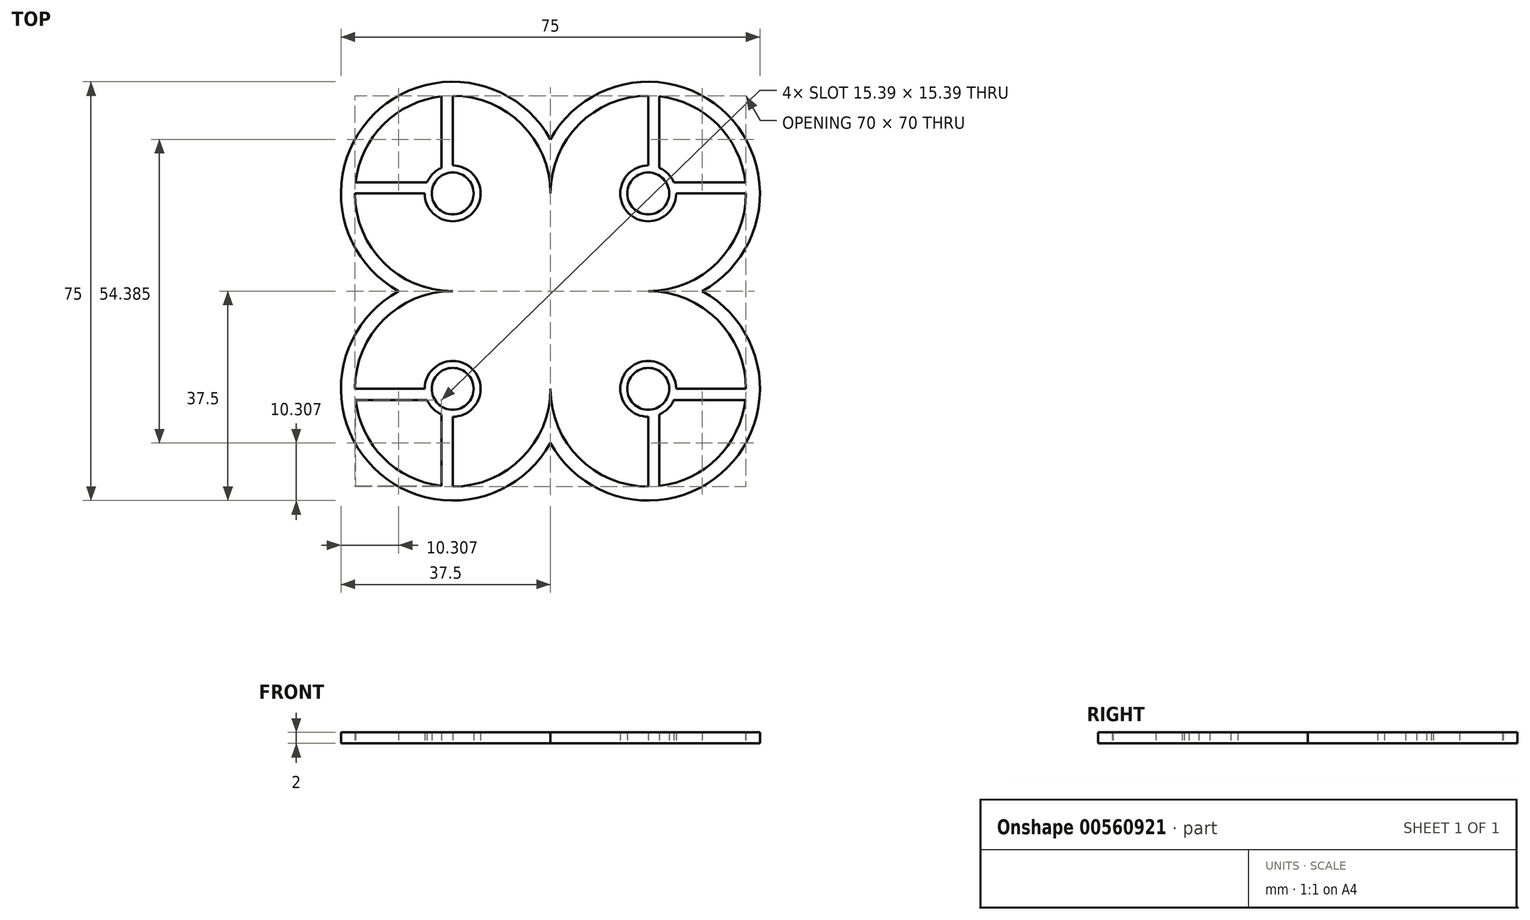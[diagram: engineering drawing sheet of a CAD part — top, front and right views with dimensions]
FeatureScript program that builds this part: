
annotation { "Feature Type Name" : "Feature", "Feature Type Description" : "" }
export const myFeature = defineFeature(function(context is Context, id is Id, definition is map)
    precondition{}
    {
        {
            var Q0;
            Q0=qCreatedBy(makeId("Top.planeOp"),FACE);
            var sketch = newSketch(context, id + "F0", { "sketchPlane" : qUnion([Q0])});
            skCircle(sketch, "E0", {"center": v(-17.5, 17.5) * mm, "radius": 17.5 * mm});
            skCircle(sketch, "E1", {"center": v(17.5, 17.5) * mm, "radius": 17.5 * mm});
            skCircle(sketch, "E2", {"center": v(-17.5, -17.5) * mm, "radius": 17.5 * mm});
            skCircle(sketch, "E3", {"center": v(17.5, -17.5) * mm, "radius": 17.5 * mm});
            skCircle(sketch, "E4", {"center": v(-17.5, 17.5) * mm, "radius": 20 * mm});
            skCircle(sketch, "E5", {"center": v(17.5, 17.5) * mm, "radius": 20 * mm});
            skCircle(sketch, "E6", {"center": v(17.5, -17.5) * mm, "radius": 20 * mm});
            skCircle(sketch, "E7", {"center": v(-17.5, -17.5) * mm, "radius": 20 * mm});
            skCircle(sketch, "E8", {"center": v(17.5, -17.5) * mm, "radius": 3.75 * mm});
            skCircle(sketch, "E9", {"center": v(17.5, 17.5) * mm, "radius": 3.75 * mm});
            skCircle(sketch, "E10", {"center": v(-17.5, 17.5) * mm, "radius": 3.75 * mm});
            skCircle(sketch, "E11", {"center": v(-17.5, -17.5) * mm, "radius": 3.75 * mm});
            skCircle(sketch, "E12", {"center": v(-17.5, -17.5) * mm, "radius": 5 * mm});
            skCircle(sketch, "E13", {"center": v(17.5, -17.5) * mm, "radius": 5 * mm});
            skCircle(sketch, "E14", {"center": v(17.5, 17.5) * mm, "radius": 5 * mm});
            skCircle(sketch, "E15", {"center": v(-17.5, 17.5) * mm, "radius": 5 * mm});
            skLineSegment(sketch, "E16.bottom", {"start": v(-17.5, 17.5) * mm, "end": v(-43.31, 17.5) * mm});
            skLineSegment(sketch, "E16.top", {"start": v(-17.5, 41.1) * mm, "end": v(-43.31, 41.1) * mm});
            skLineSegment(sketch, "E16.left", {"start": v(-17.5, 17.5) * mm, "end": v(-17.5, 41.1) * mm});
            skLineSegment(sketch, "E16.right", {"start": v(-43.31, 17.5) * mm, "end": v(-43.31, 41.1) * mm});
            skLineSegment(sketch, "E17.bottom", {"start": v(-22.08, 19.5) * mm, "end": v(-37.86, 19.5) * mm});
            skLineSegment(sketch, "E17.top", {"start": v(-19.5, 36.72) * mm, "end": v(-37.86, 36.72) * mm});
            skLineSegment(sketch, "E17.left", {"start": v(-19.5, 22.08) * mm, "end": v(-19.5, 36.72) * mm});
            skLineSegment(sketch, "E17.right", {"start": v(-37.86, 19.5) * mm, "end": v(-37.86, 36.72) * mm});
            skLineSegment(sketch, "E18.MirrorCS", {"start": v(22.08, 19.5) * mm, "end": v(37.86, 19.5) * mm});
            skLineSegment(sketch, "E19.MirrorCS", {"start": v(19.5, 22.08) * mm, "end": v(19.5, 36.72) * mm});
            skLineSegment(sketch, "E20.MirrorCS", {"start": v(-19.5, -22.08) * mm, "end": v(-19.5, -36.72) * mm});
            skLineSegment(sketch, "E21.MirrorCS", {"start": v(-22.08, -19.5) * mm, "end": v(-37.86, -19.5) * mm});
            skLineSegment(sketch, "E22.MirrorCS", {"start": v(22.08, -19.5) * mm, "end": v(37.86, -19.5) * mm});
            skLineSegment(sketch, "E23.MirrorCS", {"start": v(19.5, -22.08) * mm, "end": v(19.5, -36.72) * mm});
            skLineSegment(sketch, "E24.MirrorCS", {"start": v(17.5, 17.5) * mm, "end": v(17.5, 41.1) * mm});
            skLineSegment(sketch, "E25.MirrorCS", {"start": v(17.5, 17.5) * mm, "end": v(43.31, 17.5) * mm});
            skLineSegment(sketch, "E26.MirrorCS", {"start": v(-17.5, -17.5) * mm, "end": v(-43.31, -17.5) * mm});
            skLineSegment(sketch, "E27.MirrorCS", {"start": v(-17.5, -17.5) * mm, "end": v(-17.5, -41.1) * mm});
            skLineSegment(sketch, "E28.MirrorCS", {"start": v(17.5, -17.5) * mm, "end": v(17.5, -41.1) * mm});
            skLineSegment(sketch, "E29.MirrorCS", {"start": v(17.5, -17.5) * mm, "end": v(43.31, -17.5) * mm});
            skSolve(sketch);
        }
        {
            var Q0;
            {var subQ0=sQuery(id+"F0.wireOp",EDGE,"E5");var subQ1=sQuery(id+"F0.wireOp",EDGE,"E0");var subQ2=makeQuery(id+"F0.imprint","INTERSECT",VERTEX,{"disambiguationData":[OD(0.0)],"derivedFrom":[subQ1,subQ0]});Q0=makeQuery(id+"F0.imprint","IMPRINT",FACE,{"disambiguationData":[TD([[makeQuery(id+"F0.imprint","IMPRINT",EDGE,{"disambiguationData":[TD([[subQ2,-1.0]])],"derivedFrom":subQ1}),-1.0]])]});}
            var Q1;
            {var subQ0=sQuery(id+"F0.wireOp",EDGE,"E4");var subQ1=sQuery(id+"F0.wireOp",EDGE,"E2");var subQ2=makeQuery(id+"F0.imprint","INTERSECT",VERTEX,{"disambiguationData":[OD(1.0)],"derivedFrom":[subQ1,subQ0]});Q1=makeQuery(id+"F0.imprint","IMPRINT",FACE,{"disambiguationData":[TD([[makeQuery(id+"F0.imprint","IMPRINT",EDGE,{"disambiguationData":[TD([[subQ2,-1.0]])],"derivedFrom":subQ1}),-1.0]])]});}
            var Q2;
            {var subQ0=sQuery(id+"F0.wireOp",EDGE,"E5");var subQ1=sQuery(id+"F0.wireOp",EDGE,"E3");var subQ2=makeQuery(id+"F0.imprint","INTERSECT",VERTEX,{"disambiguationData":[OD(0.0)],"derivedFrom":[subQ1,subQ0]});Q2=makeQuery(id+"F0.imprint","IMPRINT",FACE,{"disambiguationData":[TD([[makeQuery(id+"F0.imprint","IMPRINT",EDGE,{"disambiguationData":[TD([[subQ2,1.0]])],"derivedFrom":subQ1}),-1.0]])]});}
            var Q3;
            {var subQ0=sQuery(id+"F0.wireOp",EDGE,"E4");var subQ1=sQuery(id+"F0.wireOp",EDGE,"E1");var subQ2=makeQuery(id+"F0.imprint","INTERSECT",VERTEX,{"disambiguationData":[OD(0.0)],"derivedFrom":[subQ1,subQ0]});Q3=makeQuery(id+"F0.imprint","IMPRINT",FACE,{"disambiguationData":[TD([[makeQuery(id+"F0.imprint","IMPRINT",EDGE,{"disambiguationData":[TD([[subQ2,1.0]])],"derivedFrom":subQ1}),-1.0]])]});}
            var Q4;
            {var subQ0=sQuery(id+"F0.wireOp",EDGE,"E3");var subQ1=sQuery(id+"F0.wireOp",EDGE,"E1");var subQ2=makeQuery(id+"F0.imprint","INTERSECT",VERTEX,{"derivedFrom":[subQ1,subQ0]});Q4=makeQuery(id+"F0.imprint","IMPRINT",FACE,{"disambiguationData":[TD([[makeQuery(id+"F0.imprint","IMPRINT",EDGE,{"disambiguationData":[TD([[subQ2,-1.0]])],"derivedFrom":subQ1}),-1.0]])]});}
            var Q5;
            {var subQ0=sQuery(id+"F0.wireOp",EDGE,"E3");var subQ1=sQuery(id+"F0.wireOp",EDGE,"E2");var subQ2=makeQuery(id+"F0.imprint","INTERSECT",VERTEX,{"derivedFrom":[subQ1,subQ0]});Q5=makeQuery(id+"F0.imprint","IMPRINT",FACE,{"disambiguationData":[TD([[makeQuery(id+"F0.imprint","IMPRINT",EDGE,{"disambiguationData":[TD([[subQ2,1.0]])],"derivedFrom":subQ1}),-1.0]])]});}
            var Q6;
            {var subQ0=sQuery(id+"F0.wireOp",EDGE,"E7");var subQ1=sQuery(id+"F0.wireOp",EDGE,"E0");var subQ2=makeQuery(id+"F0.imprint","INTERSECT",VERTEX,{"disambiguationData":[OD(0.0)],"derivedFrom":[subQ1,subQ0]});Q6=makeQuery(id+"F0.imprint","IMPRINT",FACE,{"disambiguationData":[TD([[makeQuery(id+"F0.imprint","IMPRINT",EDGE,{"disambiguationData":[TD([[subQ2,-1.0]])],"derivedFrom":subQ1}),-1.0]])]});}
            var Q7;
            {var subQ0=sQuery(id+"F0.wireOp",EDGE,"E5");var subQ1=sQuery(id+"F0.wireOp",EDGE,"E0");var subQ2=makeQuery(id+"F0.imprint","INTERSECT",VERTEX,{"disambiguationData":[OD(0.0)],"derivedFrom":[subQ1,subQ0]});Q7=makeQuery(id+"F0.imprint","IMPRINT",FACE,{"disambiguationData":[TD([[makeQuery(id+"F0.imprint","IMPRINT",EDGE,{"disambiguationData":[TD([[subQ2,1.0]])],"derivedFrom":subQ1}),-1.0]])]});}
            var Q8;
            {var subQ0=sQuery(id+"F0.wireOp",EDGE,"E16.bottom");var subQ1=sQuery(id+"F0.wireOp",EDGE,"E0");var subQ2=makeQuery(id+"F0.imprint","INTERSECT",VERTEX,{"derivedFrom":[subQ1,subQ0]});Q8=makeQuery(id+"F0.imprint","IMPRINT",FACE,{"disambiguationData":[TD([[makeQuery(id+"F0.imprint","IMPRINT",EDGE,{"disambiguationData":[TD([[subQ2,-1.0]])],"derivedFrom":subQ1}),-1.0]])]});}
            var Q9;
            {var subQ0=sQuery(id+"F0.wireOp",EDGE,"E17.left");var subQ5=sQuery(id+"F0.wireOp",EDGE,"E0");var subQ6=makeQuery(id+"F0.imprint","INTERSECT",VERTEX,{"derivedFrom":[subQ5,subQ0]});Q9=makeQuery(id+"F0.imprint","IMPRINT",FACE,{"disambiguationData":[TD([[makeQuery(id+"F0.imprint","IMPRINT",EDGE,{"disambiguationData":[TD([[subQ6,-1.0]])],"derivedFrom":subQ5}),-1.0]])]});}
            var Q10;
            {var subQ0=sQuery(id+"F0.wireOp",EDGE,"E17.bottom");var subQ1=sQuery(id+"F0.wireOp",EDGE,"E0");var subQ2=makeQuery(id+"F0.imprint","INTERSECT",VERTEX,{"derivedFrom":[subQ1,subQ0]});Q10=makeQuery(id+"F0.imprint","IMPRINT",FACE,{"disambiguationData":[TD([[makeQuery(id+"F0.imprint","IMPRINT",EDGE,{"disambiguationData":[TD([[subQ2,-1.0]])],"derivedFrom":subQ1}),-1.0]])]});}
            var Q11;
            {var subQ0=sQuery(id+"F0.wireOp",EDGE,"E17.bottom");var subQ1=sQuery(id+"F0.wireOp",EDGE,"E0");var subQ2=makeQuery(id+"F0.imprint","INTERSECT",VERTEX,{"derivedFrom":[subQ1,subQ0]});Q11=makeQuery(id+"F0.imprint","IMPRINT",FACE,{"disambiguationData":[TD([[makeQuery(id+"F0.imprint","IMPRINT",EDGE,{"disambiguationData":[TD([[subQ2,-1.0]])],"derivedFrom":subQ1}),1.0]])]});}
            var Q12;
            {var subQ2=sQuery(id+"F0.wireOp",EDGE,"E16.bottom");var subQ7=sQuery(id+"F0.wireOp",EDGE,"E10");var subQ9=makeQuery(id+"F0.imprint","INTERSECT",VERTEX,{"derivedFrom":[subQ7,subQ2]});Q12=makeQuery(id+"F0.imprint","IMPRINT",FACE,{"disambiguationData":[TD([[makeQuery(id+"F0.imprint","IMPRINT",EDGE,{"disambiguationData":[TD([[subQ9,1.0]])],"derivedFrom":subQ7}),-1.0]])]});}
            var Q13;
            {var subQ0=sQuery(id+"F0.wireOp",EDGE,"E16.left");var subQ1=sQuery(id+"F0.wireOp",EDGE,"E0");var subQ2=makeQuery(id+"F0.imprint","INTERSECT",VERTEX,{"derivedFrom":[subQ1,subQ0]});Q13=makeQuery(id+"F0.imprint","IMPRINT",FACE,{"disambiguationData":[TD([[makeQuery(id+"F0.imprint","IMPRINT",EDGE,{"disambiguationData":[TD([[subQ2,-1.0]])],"derivedFrom":subQ1}),1.0]])]});}
            var Q14;
            {var subQ0=sQuery(id+"F0.wireOp",EDGE,"E16.bottom");var subQ1=sQuery(id+"F0.wireOp",EDGE,"E10");var subQ2=makeQuery(id+"F0.imprint","INTERSECT",VERTEX,{"derivedFrom":[subQ1,subQ0]});Q14=makeQuery(id+"F0.imprint","IMPRINT",FACE,{"disambiguationData":[TD([[makeQuery(id+"F0.imprint","IMPRINT",EDGE,{"disambiguationData":[TD([[subQ2,-1.0]])],"derivedFrom":subQ1}),-1.0]])]});}
            var Q15;
            {var subQ5=sQuery(id+"F0.wireOp",EDGE,"E16.left");var subQ7=sQuery(id+"F0.wireOp",EDGE,"E0");var subQ8=makeQuery(id+"F0.imprint","INTERSECT",VERTEX,{"derivedFrom":[subQ7,subQ5]});Q15=makeQuery(id+"F0.imprint","IMPRINT",FACE,{"disambiguationData":[TD([[makeQuery(id+"F0.imprint","IMPRINT",EDGE,{"disambiguationData":[TD([[subQ8,-1.0]])],"derivedFrom":subQ7}),-1.0]])]});}
            var Q16;
            {var subQ0=sQuery(id+"F0.wireOp",EDGE,"E26.MirrorCS");var subQ1=sQuery(id+"F0.wireOp",EDGE,"E2");var subQ2=makeQuery(id+"F0.imprint","INTERSECT",VERTEX,{"derivedFrom":[subQ1,subQ0]});Q16=makeQuery(id+"F0.imprint","IMPRINT",FACE,{"disambiguationData":[TD([[makeQuery(id+"F0.imprint","IMPRINT",EDGE,{"disambiguationData":[TD([[subQ2,-1.0]])],"derivedFrom":subQ1}),-1.0]])]});}
            var Q17;
            {var subQ0=sQuery(id+"F0.wireOp",EDGE,"E26.MirrorCS");var subQ1=sQuery(id+"F0.wireOp",EDGE,"E2");var subQ2=makeQuery(id+"F0.imprint","INTERSECT",VERTEX,{"derivedFrom":[subQ1,subQ0]});Q17=makeQuery(id+"F0.imprint","IMPRINT",FACE,{"disambiguationData":[TD([[makeQuery(id+"F0.imprint","IMPRINT",EDGE,{"disambiguationData":[TD([[subQ2,-1.0]])],"derivedFrom":subQ1}),1.0]])]});}
            var Q18;
            {var subQ3=sQuery(id+"F0.wireOp",EDGE,"E2");var subQ5=makeQuery(id+"F0.imprint","INTERSECT",VERTEX,{"derivedFrom":[subQ3,sQuery(id+"F0.wireOp",EDGE,"E20.MirrorCS")]});Q18=makeQuery(id+"F0.imprint","IMPRINT",FACE,{"disambiguationData":[TD([[makeQuery(id+"F0.imprint","IMPRINT",EDGE,{"disambiguationData":[TD([[subQ5,1.0]])],"derivedFrom":subQ3}),-1.0]])]});}
            var Q19;
            {var subQ5=sQuery(id+"F0.wireOp",EDGE,"E26.MirrorCS");var subQ7=sQuery(id+"F0.wireOp",EDGE,"E11");var subQ8=makeQuery(id+"F0.imprint","INTERSECT",VERTEX,{"derivedFrom":[subQ7,subQ5]});Q19=makeQuery(id+"F0.imprint","IMPRINT",FACE,{"disambiguationData":[TD([[makeQuery(id+"F0.imprint","IMPRINT",EDGE,{"disambiguationData":[TD([[subQ8,-1.0]])],"derivedFrom":subQ7}),-1.0]])]});}
            var Q20;
            {var subQ0=sQuery(id+"F0.wireOp",EDGE,"E20.MirrorCS");var subQ1=sQuery(id+"F0.wireOp",EDGE,"E2");var subQ2=makeQuery(id+"F0.imprint","INTERSECT",VERTEX,{"derivedFrom":[subQ1,subQ0]});Q20=makeQuery(id+"F0.imprint","IMPRINT",FACE,{"disambiguationData":[TD([[makeQuery(id+"F0.imprint","IMPRINT",EDGE,{"disambiguationData":[TD([[subQ2,-1.0]])],"derivedFrom":subQ1}),1.0]])]});}
            var Q21;
            {var subQ0=sQuery(id+"F0.wireOp",EDGE,"E26.MirrorCS");var subQ1=sQuery(id+"F0.wireOp",EDGE,"E11");var subQ2=makeQuery(id+"F0.imprint","INTERSECT",VERTEX,{"derivedFrom":[subQ1,subQ0]});Q21=makeQuery(id+"F0.imprint","IMPRINT",FACE,{"disambiguationData":[TD([[makeQuery(id+"F0.imprint","IMPRINT",EDGE,{"disambiguationData":[TD([[subQ2,1.0]])],"derivedFrom":subQ1}),-1.0]])]});}
            var Q22;
            {var subQ0=sQuery(id+"F0.wireOp",EDGE,"E27.MirrorCS");var subQ1=sQuery(id+"F0.wireOp",EDGE,"E2");var subQ2=makeQuery(id+"F0.imprint","INTERSECT",VERTEX,{"derivedFrom":[subQ1,subQ0]});Q22=makeQuery(id+"F0.imprint","IMPRINT",FACE,{"disambiguationData":[TD([[makeQuery(id+"F0.imprint","IMPRINT",EDGE,{"disambiguationData":[TD([[subQ2,-1.0]])],"derivedFrom":subQ1}),-1.0]])]});}
            var Q23;
            {var subQ0=sQuery(id+"F0.wireOp",EDGE,"E7");var subQ1=sQuery(id+"F0.wireOp",EDGE,"E3");var subQ2=makeQuery(id+"F0.imprint","INTERSECT",VERTEX,{"disambiguationData":[OD(1.0)],"derivedFrom":[subQ1,subQ0]});Q23=makeQuery(id+"F0.imprint","IMPRINT",FACE,{"disambiguationData":[TD([[makeQuery(id+"F0.imprint","IMPRINT",EDGE,{"disambiguationData":[TD([[subQ2,-1.0]])],"derivedFrom":subQ1}),-1.0]])]});}
            var Q24;
            {var subQ3=sQuery(id+"F0.wireOp",EDGE,"E3");var subQ5=makeQuery(id+"F0.imprint","INTERSECT",VERTEX,{"derivedFrom":[subQ3,sQuery(id+"F0.wireOp",EDGE,"E23.MirrorCS")]});Q24=makeQuery(id+"F0.imprint","IMPRINT",FACE,{"disambiguationData":[TD([[makeQuery(id+"F0.imprint","IMPRINT",EDGE,{"disambiguationData":[TD([[subQ5,1.0]])],"derivedFrom":subQ3}),-1.0]])]});}
            var Q25;
            {var subQ0=sQuery(id+"F0.wireOp",EDGE,"E29.MirrorCS");var subQ1=sQuery(id+"F0.wireOp",EDGE,"E3");var subQ2=makeQuery(id+"F0.imprint","INTERSECT",VERTEX,{"derivedFrom":[subQ1,subQ0]});Q25=makeQuery(id+"F0.imprint","IMPRINT",FACE,{"disambiguationData":[TD([[makeQuery(id+"F0.imprint","IMPRINT",EDGE,{"disambiguationData":[TD([[subQ2,1.0]])],"derivedFrom":subQ1}),-1.0]])]});}
            var Q26;
            {var subQ0=sQuery(id+"F0.wireOp",EDGE,"E29.MirrorCS");var subQ1=sQuery(id+"F0.wireOp",EDGE,"E3");var subQ2=makeQuery(id+"F0.imprint","INTERSECT",VERTEX,{"derivedFrom":[subQ1,subQ0]});Q26=makeQuery(id+"F0.imprint","IMPRINT",FACE,{"disambiguationData":[TD([[makeQuery(id+"F0.imprint","IMPRINT",EDGE,{"disambiguationData":[TD([[subQ2,1.0]])],"derivedFrom":subQ1}),1.0]])]});}
            var Q27;
            {var subQ0=sQuery(id+"F0.wireOp",EDGE,"E23.MirrorCS");var subQ1=sQuery(id+"F0.wireOp",EDGE,"E3");var subQ2=makeQuery(id+"F0.imprint","INTERSECT",VERTEX,{"derivedFrom":[subQ1,subQ0]});Q27=makeQuery(id+"F0.imprint","IMPRINT",FACE,{"disambiguationData":[TD([[makeQuery(id+"F0.imprint","IMPRINT",EDGE,{"disambiguationData":[TD([[subQ2,1.0]])],"derivedFrom":subQ1}),1.0]])]});}
            var Q28;
            {var subQ4=sQuery(id+"F0.wireOp",EDGE,"E28.MirrorCS");var subQ5=sQuery(id+"F0.wireOp",EDGE,"E8");var subQ6=makeQuery(id+"F0.imprint","INTERSECT",VERTEX,{"derivedFrom":[subQ5,subQ4]});Q28=makeQuery(id+"F0.imprint","IMPRINT",FACE,{"disambiguationData":[TD([[makeQuery(id+"F0.imprint","IMPRINT",EDGE,{"disambiguationData":[TD([[subQ6,-1.0]])],"derivedFrom":subQ5}),-1.0]])]});}
            var Q29;
            {var subQ0=sQuery(id+"F0.wireOp",EDGE,"E28.MirrorCS");var subQ1=sQuery(id+"F0.wireOp",EDGE,"E8");var subQ2=makeQuery(id+"F0.imprint","INTERSECT",VERTEX,{"derivedFrom":[subQ1,subQ0]});Q29=makeQuery(id+"F0.imprint","IMPRINT",FACE,{"disambiguationData":[TD([[makeQuery(id+"F0.imprint","IMPRINT",EDGE,{"disambiguationData":[TD([[subQ2,1.0]])],"derivedFrom":subQ1}),-1.0]])]});}
            var Q30;
            {var subQ0=sQuery(id+"F0.wireOp",EDGE,"E19.MirrorCS");var subQ1=sQuery(id+"F0.wireOp",EDGE,"E1");var subQ2=makeQuery(id+"F0.imprint","INTERSECT",VERTEX,{"derivedFrom":[subQ1,subQ0]});Q30=makeQuery(id+"F0.imprint","IMPRINT",FACE,{"disambiguationData":[TD([[makeQuery(id+"F0.imprint","IMPRINT",EDGE,{"disambiguationData":[TD([[subQ2,-1.0]])],"derivedFrom":subQ1}),1.0]])]});}
            var Q31;
            {var subQ2=sQuery(id+"F0.wireOp",EDGE,"E24.MirrorCS");var subQ7=sQuery(id+"F0.wireOp",EDGE,"E9");var subQ8=makeQuery(id+"F0.imprint","INTERSECT",VERTEX,{"derivedFrom":[subQ7,subQ2]});Q31=makeQuery(id+"F0.imprint","IMPRINT",FACE,{"disambiguationData":[TD([[makeQuery(id+"F0.imprint","IMPRINT",EDGE,{"disambiguationData":[TD([[subQ8,1.0]])],"derivedFrom":subQ7}),-1.0]])]});}
            var Q32;
            {var subQ0=sQuery(id+"F0.wireOp",EDGE,"E18.MirrorCS");var subQ1=sQuery(id+"F0.wireOp",EDGE,"E1");var subQ2=makeQuery(id+"F0.imprint","INTERSECT",VERTEX,{"derivedFrom":[subQ1,subQ0]});Q32=makeQuery(id+"F0.imprint","IMPRINT",FACE,{"disambiguationData":[TD([[makeQuery(id+"F0.imprint","IMPRINT",EDGE,{"disambiguationData":[TD([[subQ2,1.0]])],"derivedFrom":subQ1}),1.0]])]});}
            var Q33;
            {var subQ3=sQuery(id+"F0.wireOp",EDGE,"E1");var subQ7=makeQuery(id+"F0.imprint","INTERSECT",VERTEX,{"derivedFrom":[subQ3,sQuery(id+"F0.wireOp",EDGE,"E19.MirrorCS")]});Q33=makeQuery(id+"F0.imprint","IMPRINT",FACE,{"disambiguationData":[TD([[makeQuery(id+"F0.imprint","IMPRINT",EDGE,{"disambiguationData":[TD([[subQ7,1.0]])],"derivedFrom":subQ3}),-1.0]])]});}
            var Q34;
            {var subQ0=sQuery(id+"F0.wireOp",EDGE,"E18.MirrorCS");var subQ1=sQuery(id+"F0.wireOp",EDGE,"E1");var subQ2=makeQuery(id+"F0.imprint","INTERSECT",VERTEX,{"derivedFrom":[subQ1,subQ0]});Q34=makeQuery(id+"F0.imprint","IMPRINT",FACE,{"disambiguationData":[TD([[makeQuery(id+"F0.imprint","IMPRINT",EDGE,{"disambiguationData":[TD([[subQ2,1.0]])],"derivedFrom":subQ1}),-1.0]])]});}
            var Q35;
            {var subQ0=sQuery(id+"F0.wireOp",EDGE,"E25.MirrorCS");var subQ1=sQuery(id+"F0.wireOp",EDGE,"E1");var subQ2=makeQuery(id+"F0.imprint","INTERSECT",VERTEX,{"derivedFrom":[subQ1,subQ0]});Q35=makeQuery(id+"F0.imprint","IMPRINT",FACE,{"disambiguationData":[TD([[makeQuery(id+"F0.imprint","IMPRINT",EDGE,{"disambiguationData":[TD([[subQ2,1.0]])],"derivedFrom":subQ1}),-1.0]])]});}
            var Q36;
            {var subQ0=sQuery(id+"F0.wireOp",EDGE,"E24.MirrorCS");var subQ1=sQuery(id+"F0.wireOp",EDGE,"E9");var subQ2=makeQuery(id+"F0.imprint","INTERSECT",VERTEX,{"derivedFrom":[subQ1,subQ0]});Q36=makeQuery(id+"F0.imprint","IMPRINT",FACE,{"disambiguationData":[TD([[makeQuery(id+"F0.imprint","IMPRINT",EDGE,{"disambiguationData":[TD([[subQ2,-1.0]])],"derivedFrom":subQ1}),-1.0]])]});}
            extrude(context, id + "F1", {"entities" : qUnion([Q0, Q1, Q2, Q3, Q4, Q5, Q6, Q7, Q8, Q9, Q10, Q11, Q12, Q13, Q14, Q15, Q16, Q17, Q18, Q19, Q20, Q21, Q22, Q23, Q24, Q25, Q26, Q27, Q28, Q29, Q30, Q31, Q32, Q33, Q34, Q35, Q36]), "depth" : 2 * mm, "offsetDistance" : 25 * mm});
        }
    });
